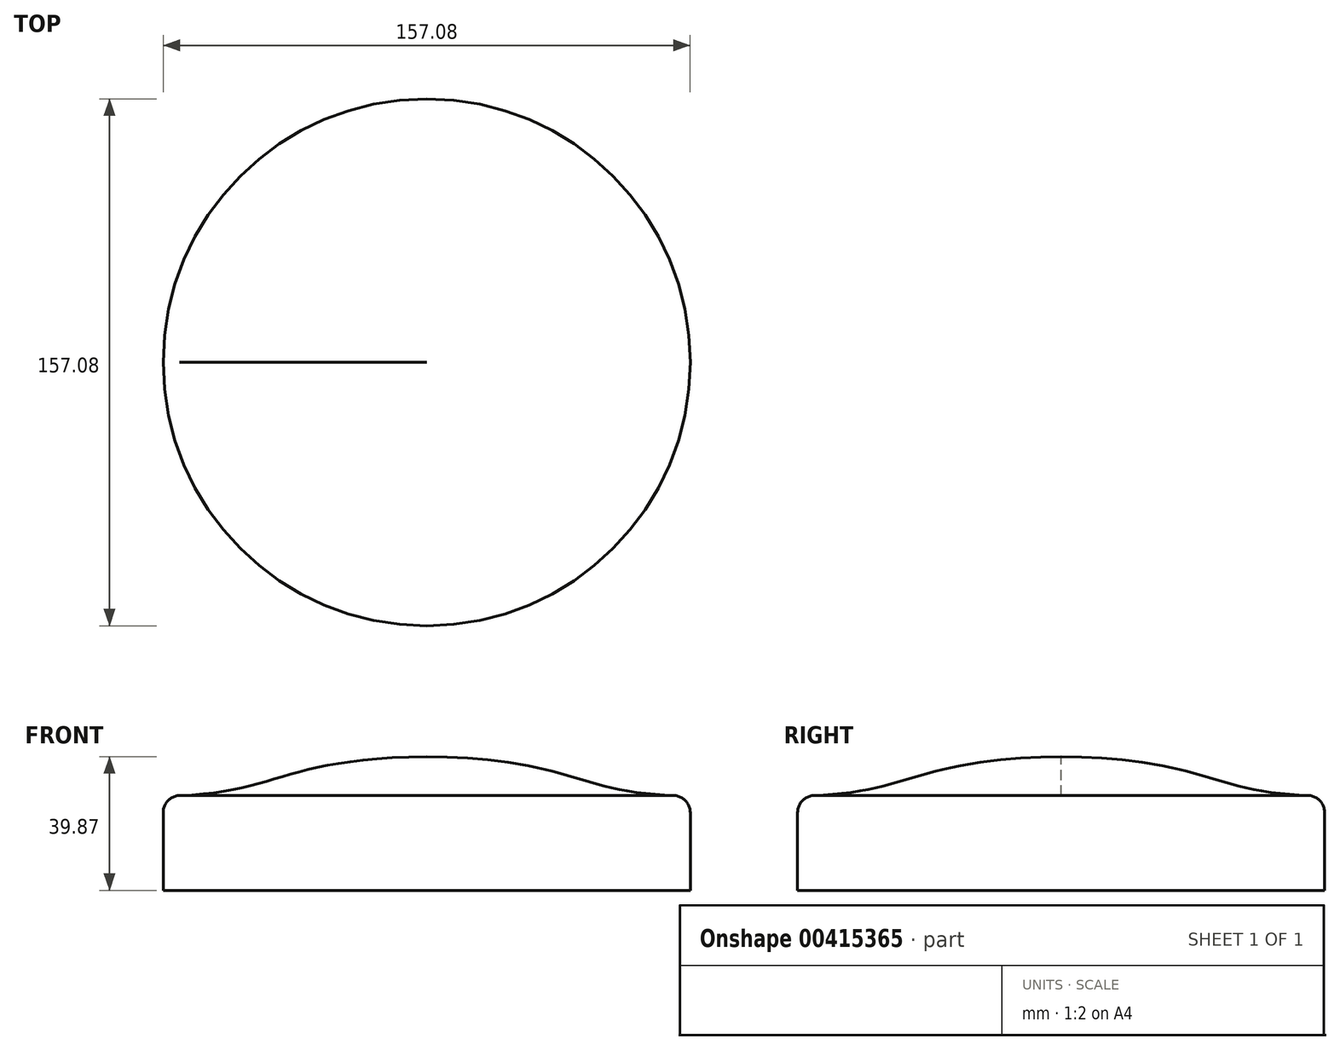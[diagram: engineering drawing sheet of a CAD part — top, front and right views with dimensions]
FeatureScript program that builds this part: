
annotation { "Feature Type Name" : "Feature", "Feature Type Description" : "" }
export const myFeature = defineFeature(function(context is Context, id is Id, definition is map)
    precondition{}
    {
        {
            var Q0;
            Q0=qCreatedBy(makeId("Front.planeOp"),FACE);
            var sketch = newSketch(context, id + "F0", { "sketchPlane" : qUnion([Q0])});
            skLineSegment(sketch, "E0.bottom", {"start": v(-78.54, 0) * mm, "end": v(0, 0) * mm});
            skLineSegment(sketch, "E0.top", {"start": v(-78.54, -28.2) * mm, "end": v(0, -28.2) * mm});
            skLineSegment(sketch, "E0.left", {"start": v(-78.54, 0) * mm, "end": v(-78.54, -28.2) * mm});
            skLineSegment(sketch, "E0.right", {"start": v(0, 0) * mm, "end": v(0, -28.2) * mm});
            skFitSpline(sketch, "E1", {"points": [v(-78.54, 0) * mm, v(0, 11.67) * mm], "startDerivative": vector(103.06, 0) * mm, "endDerivative": vector(135.53, 1.75) * mm});
            skLineSegment(sketch, "E2", {"start": v(0, 0) * mm, "end": v(0, 11.67) * mm});
            skSolve(sketch);
        }
        {
            var Q0;
            Q0=makeQuery(id+"F0.imprint","IMPRINT",FACE,{"disambiguationData":[TD([[makeQuery(id+"F0.imprint","IMPRINT",EDGE,{"derivedFrom":sQuery(id+"F0.wireOp",EDGE,"E0.bottom")}),1.0]])]});
            var Q1;
            Q1=makeQuery(id+"F0.imprint","IMPRINT",FACE,{"disambiguationData":[TD([[makeQuery(id+"F0.imprint","IMPRINT",EDGE,{"derivedFrom":sQuery(id+"F0.wireOp",EDGE,"E0.bottom")}),-1.0]])]});
            var Q2;
            Q2=sQuery(id+"F0.wireOp",EDGE,"E0.right");
            revolve(context, id + "F1", {"entities" : qUnion([Q0, Q1]), "axis" : qUnion([Q2]), "revolveType" : RevolveType.FULL});
        }
        {
            var Q0;
            Q0=makeQuery(id+"F1.opRevolve","SWEPT_EDGE",EDGE,{"disambiguationData":[OSD([sQuery(id+"F0.wireOp",EDGE,"E0.bottom"),sQuery(id+"F0.wireOp",EDGE,"E0.left"),sQuery(id+"F0.wireOp",EDGE,"E1")])]});
            fillet(context, id + "F2", {"entities" : qUnion([Q0]), "radius" : 5.08 * mm, "tangentPropagation" : true, "allowEdgeOverflow" : false});
        }
    });
